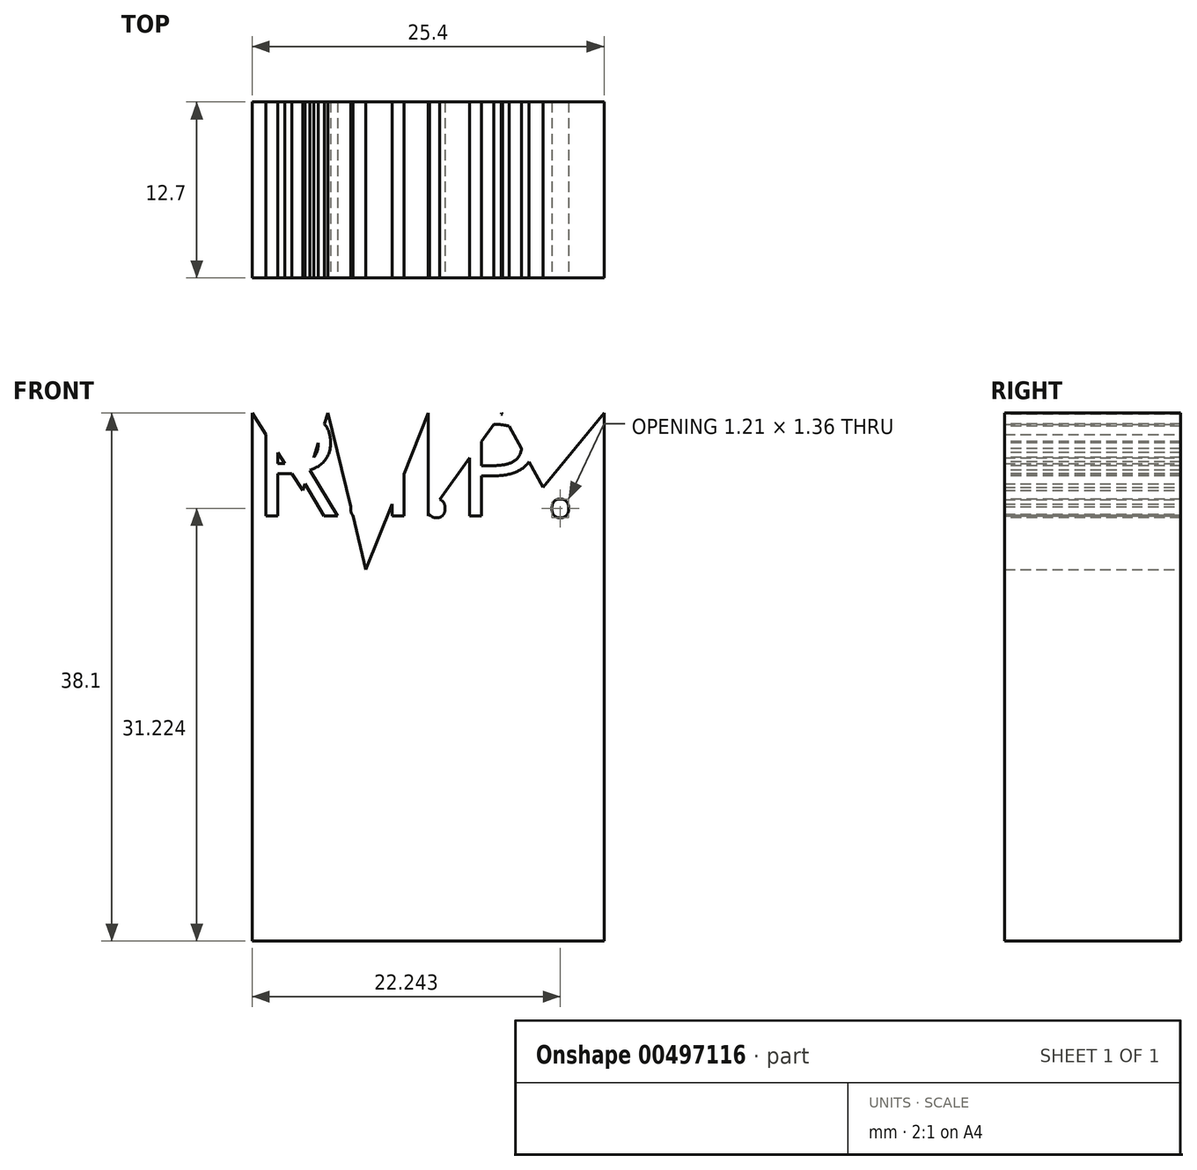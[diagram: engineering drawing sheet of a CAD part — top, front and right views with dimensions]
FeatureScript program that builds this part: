
annotation { "Feature Type Name" : "Feature", "Feature Type Description" : "" }
export const myFeature = defineFeature(function(context is Context, id is Id, definition is map)
    precondition{}
    {
        {
            var Q0;
            Q0=qCreatedBy(makeId("Front.planeOp"),FACE);
            var sketch = newSketch(context, id + "F0", { "sketchPlane" : qUnion([Q0])});
            skLineSegment(sketch, "E0", {"start": v(-12.7, 10.55) * mm, "end": v(-12.7, 48.65) * mm});
            skLineSegment(sketch, "E1.MirrorCS", {"start": v(12.7, 10.55) * mm, "end": v(12.7, 48.65) * mm});
            skLineSegment(sketch, "E2", {"start": v(-12.7, 10.55) * mm, "end": v(12.7, 10.55) * mm});
            skLineSegment(sketch, "E3", {"start": v(-12.7, 48.65) * mm, "end": v(-9.04, 43.07) * mm});
            skLineSegment(sketch, "E4", {"start": v(-9.04, 43.07) * mm, "end": v(-7.22, 48.65) * mm});
            skLineSegment(sketch, "E5", {"start": v(-7.22, 48.65) * mm, "end": v(-4.48, 37.37) * mm});
            skLineSegment(sketch, "E6", {"start": v(-4.48, 37.37) * mm, "end": v(0, 48.65) * mm});
            skLineSegment(sketch, "E7", {"start": v(0, 48.65) * mm, "end": v(0, 41.24) * mm});
            skLineSegment(sketch, "E8", {"start": v(0, 41.24) * mm, "end": v(5.32, 48.65) * mm});
            skLineSegment(sketch, "E9", {"start": v(5.32, 48.65) * mm, "end": v(8.29, 43.3) * mm});
            skLineSegment(sketch, "E10", {"start": v(8.29, 43.3) * mm, "end": v(12.7, 48.65) * mm});
            skSolve(sketch);
        }
        {
            var Q0;
            Q0=makeQuery(id+"F0.imprint","IMPRINT",FACE,{"disambiguationData":[TD([[makeQuery(id+"F0.imprint","IMPRINT",EDGE,{"derivedFrom":sQuery(id+"F0.wireOp",EDGE,"E0")}),-1.0]])]});
            extrude(context, id + "F1", {"entities" : qUnion([Q0]), "depth" : 12.7 * mm});
        }
        {
            var Q0;
            Q0=makeQuery(id+"F1.opExtrude","CAP_FACE",FACE,{"disambiguationData":[OSD([sQuery(id+"F0.wireOp",EDGE,"E0"),sQuery(id+"F0.wireOp",EDGE,"E1.MirrorCS"),sQuery(id+"F0.wireOp",EDGE,"E2"),sQuery(id+"F0.wireOp",EDGE,"E3"),sQuery(id+"F0.wireOp",EDGE,"E4"),sQuery(id+"F0.wireOp",EDGE,"E5"),sQuery(id+"F0.wireOp",EDGE,"E6"),sQuery(id+"F0.wireOp",EDGE,"E7"),sQuery(id+"F0.wireOp",EDGE,"E8"),sQuery(id+"F0.wireOp",EDGE,"E9"),sQuery(id+"F0.wireOp",EDGE,"E10")])],"isStart":false});
            var sketch = newSketch(context, id + "F2", { "sketchPlane" : qUnion([Q0])});
            skPoint(sketch, "E11.firstSnap0", {"position": v(-8.13, 45.86) * mm});
            skText(sketch, "E12", { "text": "R.I.P.", "fontName": "OpenSans-Regular.ttf"});
            const initialGuessF2  = {"E12": [-0.0127, 0.04124, 1, 0, 0.0074]};
            skSetInitialGuess(sketch, initialGuessF2);
            skSolve(sketch);
        }
        {
            var Q0;
            Q0 = qSketchRegion(id + "F2", true);
            extrude(context, id + "F3", {"entities" : qUnion([Q0]), "operationType" : NewBodyOperationType.REMOVE, "oppositeDirection" : true, "depth" : 25.4 * mm});
        }
    });
